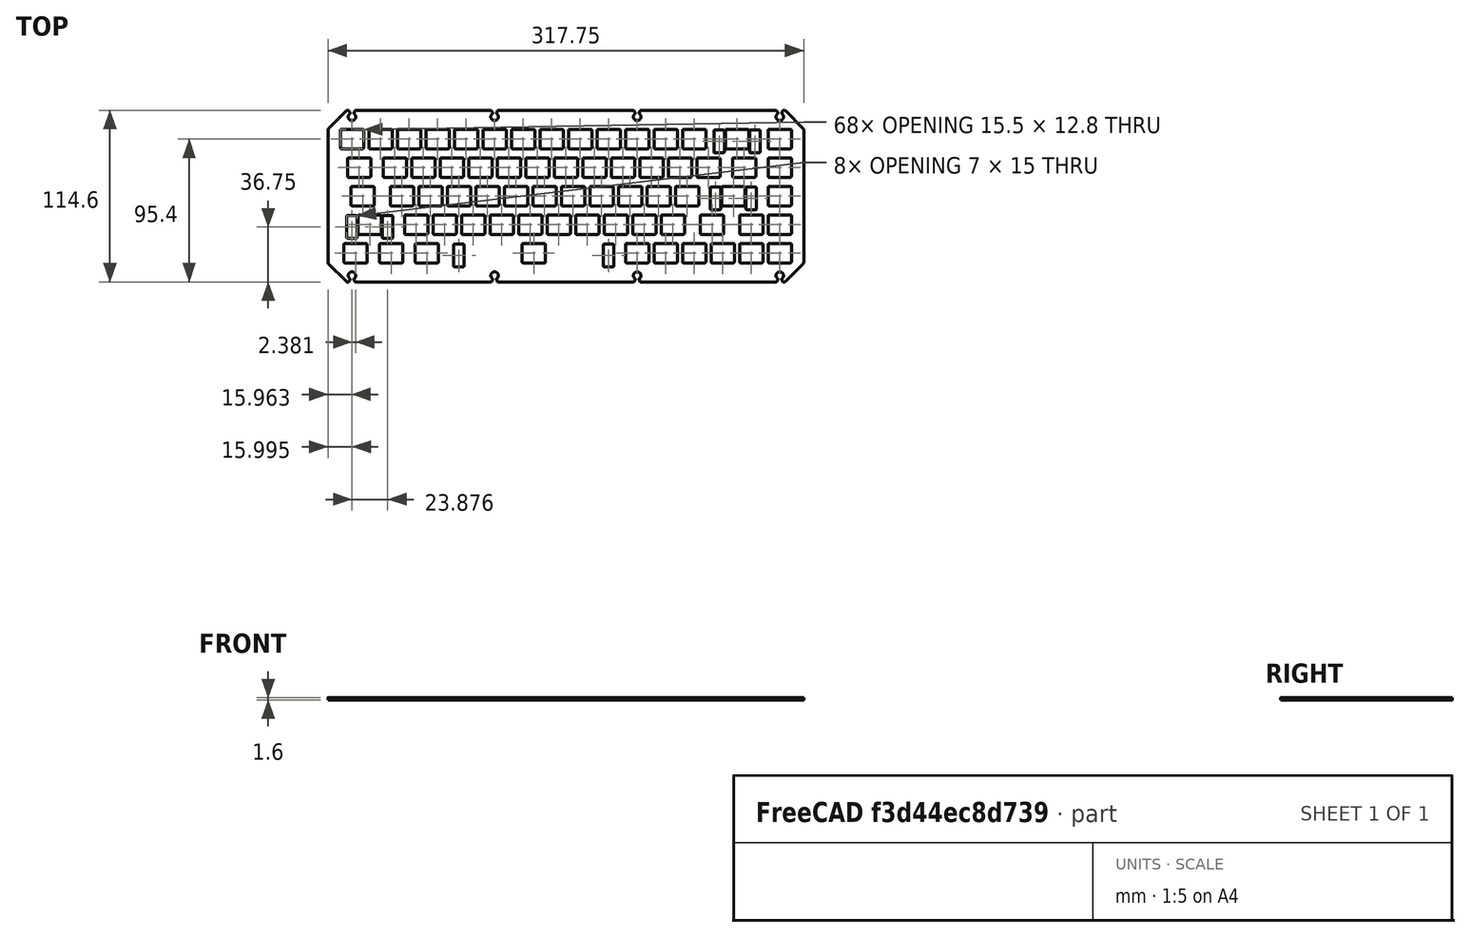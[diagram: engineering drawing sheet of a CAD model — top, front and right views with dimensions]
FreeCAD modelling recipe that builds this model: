
FCSTD DOCUMENT  (FreeCAD 0.21R33771 (Git))
Label: plate_merged
License: All rights reserved
LicenseURL: https://en.wikipedia.org/wiki/All_rights_reserved
objects: Sketcher::SketchObject×1, PartDesign::Pad×1, PartDesign::Body×1
note: 4 computed .brp shape members not serialized (recipe doc carries the construction recipe); baked Part::Feature solids carry a one-line shape summary decoded from their .brp

FEATURE [Sketcher::SketchObject] Sketch
  FullyConstrained = false
  MapMode = 5
  Support = -> [XY_Plane]
  sketch-geometry (688):
    g0: ArcOfCircle CenterX=-150.125 CenterY=44 CenterZ=0 NormalX=0 NormalY=0 NormalZ=1 AngleXU=0 Radius=0.5 StartAngle=1.5708 EndAngle=3.14159
    g1: LineSegment StartX=-150.125 StartY=44.5 StartZ=0 EndX=-135.625 EndY=44.5 EndZ=0
    g2: ArcOfCircle CenterX=-135.625 CenterY=44 CenterZ=0 NormalX=0 NormalY=0 NormalZ=1 AngleXU=0 Radius=0.5 StartAngle=0 EndAngle=1.5708
    g3: LineSegment StartX=-135.125 StartY=44 StartZ=0 EndX=-135.125 EndY=32.2 EndZ=0
    g4: ArcOfCircle CenterX=-135.625 CenterY=32.2 CenterZ=0 NormalX=0 NormalY=0 NormalZ=1 AngleXU=0 Radius=0.5 StartAngle=4.71239 EndAngle=6.28319
    g5: LineSegment StartX=-150.125 StartY=31.7 StartZ=0 EndX=-135.625 EndY=31.7 EndZ=0
    g6: ArcOfCircle CenterX=-150.125 CenterY=32.2 CenterZ=0 NormalX=0 NormalY=0 NormalZ=1 AngleXU=0 Radius=0.5 StartAngle=3.14159 EndAngle=4.71239
    g7: LineSegment StartX=-150.625 StartY=44 StartZ=0 EndX=-150.625 EndY=32.2 EndZ=0
    g8: ArcOfCircle CenterX=-131.075 CenterY=44 CenterZ=0 NormalX=0 NormalY=0 NormalZ=1 AngleXU=0 Radius=0.5 StartAngle=1.5708 EndAngle=3.14159
    g9: LineSegment StartX=-131.075 StartY=44.5 StartZ=0 EndX=-116.575 EndY=44.5 EndZ=0
    g10: ArcOfCircle CenterX=-116.575 CenterY=44 CenterZ=0 NormalX=0 NormalY=0 NormalZ=1 AngleXU=0 Radius=0.5 StartAngle=0 EndAngle=1.5708
    g11: LineSegment StartX=-116.075 StartY=44 StartZ=0 EndX=-116.075 EndY=32.2 EndZ=0
    g12: ArcOfCircle CenterX=-116.575 CenterY=32.2 CenterZ=0 NormalX=0 NormalY=0 NormalZ=1 AngleXU=0 Radius=0.5 StartAngle=4.71239 EndAngle=6.28319
    g13: LineSegment StartX=-131.075 StartY=31.7 StartZ=0 EndX=-116.575 EndY=31.7 EndZ=0
    g14: ArcOfCircle CenterX=-131.075 CenterY=32.2 CenterZ=0 NormalX=0 NormalY=0 NormalZ=1 AngleXU=0 Radius=0.5 StartAngle=3.14159 EndAngle=4.71239
    g15: LineSegment StartX=-131.575 StartY=44 StartZ=0 EndX=-131.575 EndY=32.2 EndZ=0
    g16: ArcOfCircle CenterX=-112.025 CenterY=44 CenterZ=0 NormalX=0 NormalY=0 NormalZ=1 AngleXU=0 Radius=0.5 StartAngle=1.5708 EndAngle=3.14159
    g17: LineSegment StartX=-112.025 StartY=44.5 StartZ=0 EndX=-97.525 EndY=44.5 EndZ=0
    g18: ArcOfCircle CenterX=-97.525 CenterY=44 CenterZ=0 NormalX=0 NormalY=0 NormalZ=1 AngleXU=0 Radius=0.5 StartAngle=0 EndAngle=1.5708
    g19: LineSegment StartX=-97.025 StartY=44 StartZ=0 EndX=-97.025 EndY=32.2 EndZ=0
    g20: ArcOfCircle CenterX=-97.525 CenterY=32.2 CenterZ=0 NormalX=0 NormalY=0 NormalZ=1 AngleXU=0 Radius=0.5 StartAngle=4.71239 EndAngle=6.28319
    g21: LineSegment StartX=-112.025 StartY=31.7 StartZ=0 EndX=-97.525 EndY=31.7 EndZ=0
    g22: ArcOfCircle CenterX=-112.025 CenterY=32.2 CenterZ=0 NormalX=0 NormalY=0 NormalZ=1 AngleXU=0 Radius=0.5 StartAngle=3.14159 EndAngle=4.71239
    g23: LineSegment StartX=-112.525 StartY=44 StartZ=0 EndX=-112.525 EndY=32.2 EndZ=0
    g24: ArcOfCircle CenterX=-92.975 CenterY=44 CenterZ=0 NormalX=0 NormalY=0 NormalZ=1 AngleXU=0 Radius=0.5 StartAngle=1.5708 EndAngle=3.14159
    g25: LineSegment StartX=-92.975 StartY=44.5 StartZ=0 EndX=-78.475 EndY=44.5 EndZ=0
    g26: ArcOfCircle CenterX=-78.475 CenterY=44 CenterZ=0 NormalX=0 NormalY=0 NormalZ=1 AngleXU=0 Radius=0.5 StartAngle=0 EndAngle=1.5708
    g27: LineSegment StartX=-77.975 StartY=44 StartZ=0 EndX=-77.975 EndY=32.2 EndZ=0
    g28: ArcOfCircle CenterX=-78.475 CenterY=32.2 CenterZ=0 NormalX=0 NormalY=0 NormalZ=1 AngleXU=0 Radius=0.5 StartAngle=4.71239 EndAngle=6.28319
    g29: LineSegment StartX=-92.975 StartY=31.7 StartZ=0 EndX=-78.475 EndY=31.7 EndZ=0
    g30: ArcOfCircle CenterX=-92.975 CenterY=32.2 CenterZ=0 NormalX=0 NormalY=0 NormalZ=1 AngleXU=0 Radius=0.5 StartAngle=3.14159 EndAngle=4.71239
    g31: LineSegment StartX=-93.475 StartY=44 StartZ=0 EndX=-93.475 EndY=32.2 EndZ=0
    g32: ArcOfCircle CenterX=-73.925 CenterY=44 CenterZ=0 NormalX=0 NormalY=0 NormalZ=1 AngleXU=0 Radius=0.5 StartAngle=1.5708 EndAngle=3.14159
    g33: LineSegment StartX=-73.925 StartY=44.5 StartZ=0 EndX=-59.425 EndY=44.5 EndZ=0
    g34: ArcOfCircle CenterX=-59.425 CenterY=44 CenterZ=0 NormalX=0 NormalY=0 NormalZ=1 AngleXU=0 Radius=0.5 StartAngle=0 EndAngle=1.5708
    g35: LineSegment StartX=-58.925 StartY=44 StartZ=0 EndX=-58.925 EndY=32.2 EndZ=0
    g36: ArcOfCircle CenterX=-59.425 CenterY=32.2 CenterZ=0 NormalX=0 NormalY=0 NormalZ=1 AngleXU=0 Radius=0.5 StartAngle=4.71239 EndAngle=6.28319
    g37: LineSegment StartX=-73.925 StartY=31.7 StartZ=0 EndX=-59.425 EndY=31.7 EndZ=0
    g38: ArcOfCircle CenterX=-73.925 CenterY=32.2 CenterZ=0 NormalX=0 NormalY=0 NormalZ=1 AngleXU=0 Radius=0.5 StartAngle=3.14159 EndAngle=4.71239
    g39: LineSegment StartX=-74.425 StartY=44 StartZ=0 EndX=-74.425 EndY=32.2 EndZ=0
    g40: ArcOfCircle CenterX=-54.875 CenterY=44 CenterZ=0 NormalX=0 NormalY=0 NormalZ=1 AngleXU=0 Radius=0.5 StartAngle=1.5708 EndAngle=3.14159
    g41: LineSegment StartX=-54.875 StartY=44.5 StartZ=0 EndX=-40.375 EndY=44.5 EndZ=0
    g42: ArcOfCircle CenterX=-40.375 CenterY=44 CenterZ=0 NormalX=0 NormalY=0 NormalZ=1 AngleXU=0 Radius=0.5 StartAngle=0 EndAngle=1.5708
    g43: LineSegment StartX=-39.875 StartY=44 StartZ=0 EndX=-39.875 EndY=32.2 EndZ=0
    g44: ArcOfCircle CenterX=-40.375 CenterY=32.2 CenterZ=0 NormalX=0 NormalY=0 NormalZ=1 AngleXU=0 Radius=0.5 StartAngle=4.71239 EndAngle=6.28319
    g45: LineSegment StartX=-54.875 StartY=31.7 StartZ=0 EndX=-40.375 EndY=31.7 EndZ=0
    g46: ArcOfCircle CenterX=-54.875 CenterY=32.2 CenterZ=0 NormalX=0 NormalY=0 NormalZ=1 AngleXU=0 Radius=0.5 StartAngle=3.14159 EndAngle=4.71239
    g47: LineSegment StartX=-55.375 StartY=44 StartZ=0 EndX=-55.375 EndY=32.2 EndZ=0
    g48: ArcOfCircle CenterX=-35.825 CenterY=44 CenterZ=0 NormalX=0 NormalY=0 NormalZ=1 AngleXU=0 Radius=0.5 StartAngle=1.5708 EndAngle=3.14159
    g49: LineSegment StartX=-35.825 StartY=44.5 StartZ=0 EndX=-21.325 EndY=44.5 EndZ=0
    g50: ArcOfCircle CenterX=-21.325 CenterY=44 CenterZ=0 NormalX=0 NormalY=0 NormalZ=1 AngleXU=0 Radius=0.5 StartAngle=0 EndAngle=1.5708
    g51: LineSegment StartX=-20.825 StartY=44 StartZ=0 EndX=-20.825 EndY=32.2 EndZ=0
    g52: ArcOfCircle CenterX=-21.325 CenterY=32.2 CenterZ=0 NormalX=0 NormalY=0 NormalZ=1 AngleXU=0 Radius=0.5 StartAngle=4.71239 EndAngle=6.28319
    g53: LineSegment StartX=-35.825 StartY=31.7 StartZ=0 EndX=-21.325 EndY=31.7 EndZ=0
    g54: ArcOfCircle CenterX=-35.825 CenterY=32.2 CenterZ=0 NormalX=0 NormalY=0 NormalZ=1 AngleXU=0 Radius=0.5 StartAngle=3.14159 EndAngle=4.71239
    g55: LineSegment StartX=-36.325 StartY=44 StartZ=0 EndX=-36.325 EndY=32.2 EndZ=0
    g56: ArcOfCircle CenterX=-16.775 CenterY=44 CenterZ=0 NormalX=0 NormalY=0 NormalZ=1 AngleXU=0 Radius=0.5 StartAngle=1.5708 EndAngle=3.14159
    g57: LineSegment StartX=-16.775 StartY=44.5 StartZ=0 EndX=-2.275 EndY=44.5 EndZ=0
    g58: ArcOfCircle CenterX=-2.275 CenterY=44 CenterZ=0 NormalX=0 NormalY=0 NormalZ=1 AngleXU=0 Radius=0.5 StartAngle=0 EndAngle=1.5708
    g59: LineSegment StartX=-1.775 StartY=44 StartZ=0 EndX=-1.775 EndY=32.2 EndZ=0
    g60: ArcOfCircle CenterX=-2.275 CenterY=32.2 CenterZ=0 NormalX=0 NormalY=0 NormalZ=1 AngleXU=0 Radius=0.5 StartAngle=4.71239 EndAngle=6.28319
    g61: LineSegment StartX=-16.775 StartY=31.7 StartZ=0 EndX=-2.275 EndY=31.7 EndZ=0
    g62: ArcOfCircle CenterX=-16.775 CenterY=32.2 CenterZ=0 NormalX=0 NormalY=0 NormalZ=1 AngleXU=0 Radius=0.5 StartAngle=3.14159 EndAngle=4.71239
    g63: LineSegment StartX=-17.275 StartY=44 StartZ=0 EndX=-17.275 EndY=32.2 EndZ=0
    g64: ArcOfCircle CenterX=2.275 CenterY=44 CenterZ=0 NormalX=0 NormalY=0 NormalZ=1 AngleXU=0 Radius=0.5 StartAngle=1.5708 EndAngle=3.14159
    g65: LineSegment StartX=2.275 StartY=44.5 StartZ=0 EndX=16.775 EndY=44.5 EndZ=0
    g66: ArcOfCircle CenterX=16.775 CenterY=44 CenterZ=0 NormalX=0 NormalY=0 NormalZ=1 AngleXU=0 Radius=0.5 StartAngle=0 EndAngle=1.5708
    g67: LineSegment StartX=17.275 StartY=44 StartZ=0 EndX=17.275 EndY=32.2 EndZ=0
    g68: ArcOfCircle CenterX=16.775 CenterY=32.2 CenterZ=0 NormalX=0 NormalY=0 NormalZ=1 AngleXU=0 Radius=0.5 StartAngle=4.71239 EndAngle=6.28319
    g69: LineSegment StartX=2.275 StartY=31.7 StartZ=0 EndX=16.775 EndY=31.7 EndZ=0
    g70: ArcOfCircle CenterX=2.275 CenterY=32.2 CenterZ=0 NormalX=0 NormalY=0 NormalZ=1 AngleXU=0 Radius=0.5 StartAngle=3.14159 EndAngle=4.71239
    g71: LineSegment StartX=1.775 StartY=44 StartZ=0 EndX=1.775 EndY=32.2 EndZ=0
    g72: ArcOfCircle CenterX=21.325 CenterY=44 CenterZ=0 NormalX=0 NormalY=0 NormalZ=1 AngleXU=0 Radius=0.5 StartAngle=1.5708 EndAngle=3.14159
    g73: LineSegment StartX=21.325 StartY=44.5 StartZ=0 EndX=35.825 EndY=44.5 EndZ=0
    g74: ArcOfCircle CenterX=35.825 CenterY=44 CenterZ=0 NormalX=0 NormalY=0 NormalZ=1 AngleXU=0 Radius=0.5 StartAngle=0 EndAngle=1.5708
    g75: LineSegment StartX=36.325 StartY=44 StartZ=0 EndX=36.325 EndY=32.2 EndZ=0
    g76: ArcOfCircle CenterX=35.825 CenterY=32.2 CenterZ=0 NormalX=0 NormalY=0 NormalZ=1 AngleXU=0 Radius=0.5 StartAngle=4.71239 EndAngle=6.28319
    g77: LineSegment StartX=21.325 StartY=31.7 StartZ=0 EndX=35.825 EndY=31.7 EndZ=0
    g78: ArcOfCircle CenterX=21.325 CenterY=32.2 CenterZ=0 NormalX=0 NormalY=0 NormalZ=1 AngleXU=0 Radius=0.5 StartAngle=3.14159 EndAngle=4.71239
    g79: LineSegment StartX=20.825 StartY=44 StartZ=0 EndX=20.825 EndY=32.2 EndZ=0
    g80: ArcOfCircle CenterX=40.375 CenterY=44 CenterZ=0 NormalX=0 NormalY=0 NormalZ=1 AngleXU=0 Radius=0.5 StartAngle=1.5708 EndAngle=3.14159
    g81: LineSegment StartX=40.375 StartY=44.5 StartZ=0 EndX=54.875 EndY=44.5 EndZ=0
    g82: ArcOfCircle CenterX=54.875 CenterY=44 CenterZ=0 NormalX=0 NormalY=0 NormalZ=1 AngleXU=0 Radius=0.5 StartAngle=0 EndAngle=1.5708
    g83: LineSegment StartX=55.375 StartY=44 StartZ=0 EndX=55.375 EndY=32.2 EndZ=0
    g84: ArcOfCircle CenterX=54.875 CenterY=32.2 CenterZ=0 NormalX=0 NormalY=0 NormalZ=1 AngleXU=0 Radius=0.5 StartAngle=4.71239 EndAngle=6.28319
    g85: LineSegment StartX=40.375 StartY=31.7 StartZ=0 EndX=54.875 EndY=31.7 EndZ=0
    g86: ArcOfCircle CenterX=40.375 CenterY=32.2 CenterZ=0 NormalX=0 NormalY=0 NormalZ=1 AngleXU=0 Radius=0.5 StartAngle=3.14159 EndAngle=4.71239
    g87: LineSegment StartX=39.875 StartY=44 StartZ=0 EndX=39.875 EndY=32.2 EndZ=0
    g88: ArcOfCircle CenterX=59.425 CenterY=44 CenterZ=0 NormalX=0 NormalY=0 NormalZ=1 AngleXU=0 Radius=0.5 StartAngle=1.5708 EndAngle=3.14159
    g89: LineSegment StartX=59.425 StartY=44.5 StartZ=0 EndX=73.925 EndY=44.5 EndZ=0
    g90: ArcOfCircle CenterX=73.925 CenterY=44 CenterZ=0 NormalX=0 NormalY=0 NormalZ=1 AngleXU=0 Radius=0.5 StartAngle=0 EndAngle=1.5708
    g91: LineSegment StartX=74.425 StartY=44 StartZ=0 EndX=74.425 EndY=32.2 EndZ=0
    g92: ArcOfCircle CenterX=73.925 CenterY=32.2 CenterZ=0 NormalX=0 NormalY=0 NormalZ=1 AngleXU=0 Radius=0.5 StartAngle=4.71239 EndAngle=6.28319
    g93: LineSegment StartX=59.425 StartY=31.7 StartZ=0 EndX=73.925 EndY=31.7 EndZ=0
    g94: ArcOfCircle CenterX=59.425 CenterY=32.2 CenterZ=0 NormalX=0 NormalY=0 NormalZ=1 AngleXU=0 Radius=0.5 StartAngle=3.14159 EndAngle=4.71239
    g95: LineSegment StartX=58.925 StartY=44 StartZ=0 EndX=58.925 EndY=32.2 EndZ=0
    g96: ArcOfCircle CenterX=78.475 CenterY=44 CenterZ=0 NormalX=0 NormalY=0 NormalZ=1 AngleXU=0 Radius=0.5 StartAngle=1.5708 EndAngle=3.14159
    g97: LineSegment StartX=78.475 StartY=44.5 StartZ=0 EndX=92.975 EndY=44.5 EndZ=0
    g98: ArcOfCircle CenterX=92.975 CenterY=44 CenterZ=0 NormalX=0 NormalY=0 NormalZ=1 AngleXU=0 Radius=0.5 StartAngle=0 EndAngle=1.5708
    g99: LineSegment StartX=93.475 StartY=44 StartZ=0 EndX=93.475 EndY=32.2 EndZ=0
    g100: ArcOfCircle CenterX=92.975 CenterY=32.2 CenterZ=0 NormalX=0 NormalY=0 NormalZ=1 AngleXU=0 Radius=0.5 StartAngle=4.71239 EndAngle=6.28319
    g101: LineSegment StartX=78.475 StartY=31.7 StartZ=0 EndX=92.975 EndY=31.7 EndZ=0
    g102: ArcOfCircle CenterX=78.475 CenterY=32.2 CenterZ=0 NormalX=0 NormalY=0 NormalZ=1 AngleXU=0 Radius=0.5 StartAngle=3.14159 EndAngle=4.71239
    g103: LineSegment StartX=77.975 StartY=44 StartZ=0 EndX=77.975 EndY=32.2 EndZ=0
    g104: ArcOfCircle CenterX=107.05 CenterY=44 CenterZ=0 NormalX=0 NormalY=0 NormalZ=1 AngleXU=0 Radius=0.5 StartAngle=1.5708 EndAngle=3.14159
    g105: LineSegment StartX=107.05 StartY=44.5 StartZ=0 EndX=121.55 EndY=44.5 EndZ=0
    g106: ArcOfCircle CenterX=121.55 CenterY=44 CenterZ=0 NormalX=0 NormalY=0 NormalZ=1 AngleXU=0 Radius=0.5 StartAngle=0 EndAngle=1.5708
    g107: LineSegment StartX=122.05 StartY=44 StartZ=0 EndX=122.05 EndY=32.2 EndZ=0
    g108: ArcOfCircle CenterX=121.55 CenterY=32.2 CenterZ=0 NormalX=0 NormalY=0 NormalZ=1 AngleXU=0 Radius=0.5 StartAngle=4.71239 EndAngle=6.28319
    g109: LineSegment StartX=107.05 StartY=31.7 StartZ=0 EndX=121.55 EndY=31.7 EndZ=0
    g110: ArcOfCircle CenterX=107.05 CenterY=32.2 CenterZ=0 NormalX=0 NormalY=0 NormalZ=1 AngleXU=0 Radius=0.5 StartAngle=3.14159 EndAngle=4.71239
    g111: LineSegment StartX=106.55 StartY=44 StartZ=0 EndX=106.55 EndY=32.2 EndZ=0
    g112: ArcOfCircle CenterX=99.362 CenterY=43.6 CenterZ=0 NormalX=0 NormalY=0 NormalZ=1 AngleXU=0 Radius=0.5 StartAngle=1.5708 EndAngle=3.14159
    g113: LineSegment StartX=99.362 StartY=44.1 StartZ=0 EndX=105.362 EndY=44.1 EndZ=0
    g114: ArcOfCircle CenterX=105.362 CenterY=43.6 CenterZ=0 NormalX=0 NormalY=0 NormalZ=1 AngleXU=0 Radius=0.5 StartAngle=0 EndAngle=1.5708
    g115: LineSegment StartX=105.862 StartY=43.6 StartZ=0 EndX=105.862 EndY=29.6 EndZ=0
    g116: ArcOfCircle CenterX=105.362 CenterY=29.6 CenterZ=0 NormalX=0 NormalY=0 NormalZ=1 AngleXU=0 Radius=0.5 StartAngle=4.71239 EndAngle=6.28319
    g117: LineSegment StartX=99.362 StartY=29.1 StartZ=0 EndX=105.362 EndY=29.1 EndZ=0
    g118: ArcOfCircle CenterX=99.362 CenterY=29.6 CenterZ=0 NormalX=0 NormalY=0 NormalZ=1 AngleXU=0 Radius=0.5 StartAngle=3.14159 EndAngle=4.71239
    g119: LineSegment StartX=98.862 StartY=43.6 StartZ=0 EndX=98.862 EndY=29.6 EndZ=0
    g120: ArcOfCircle CenterX=123.238 CenterY=43.6 CenterZ=0 NormalX=0 NormalY=0 NormalZ=1 AngleXU=0 Radius=0.5 StartAngle=1.5708 EndAngle=3.14159
    g121: LineSegment StartX=123.238 StartY=44.1 StartZ=0 EndX=129.238 EndY=44.1 EndZ=0
    g122: ArcOfCircle CenterX=129.238 CenterY=43.6 CenterZ=0 NormalX=0 NormalY=0 NormalZ=1 AngleXU=0 Radius=0.5 StartAngle=0 EndAngle=1.5708
    g123: LineSegment StartX=129.738 StartY=43.6 StartZ=0 EndX=129.738 EndY=29.6 EndZ=0
    g124: ArcOfCircle CenterX=129.238 CenterY=29.6 CenterZ=0 NormalX=0 NormalY=0 NormalZ=1 AngleXU=0 Radius=0.5 StartAngle=4.71239 EndAngle=6.28319
    g125: LineSegment StartX=123.238 StartY=29.1 StartZ=0 EndX=129.238 EndY=29.1 EndZ=0
    g126: ArcOfCircle CenterX=123.238 CenterY=29.6 CenterZ=0 NormalX=0 NormalY=0 NormalZ=1 AngleXU=0 Radius=0.5 StartAngle=3.14159 EndAngle=4.71239
    g127: LineSegment StartX=122.738 StartY=43.6 StartZ=0 EndX=122.738 EndY=29.6 EndZ=0
    g128: ArcOfCircle CenterX=135.625 CenterY=44 CenterZ=0 NormalX=0 NormalY=0 NormalZ=1 AngleXU=0 Radius=0.5 StartAngle=1.5708 EndAngle=3.14159
    g129: LineSegment StartX=135.625 StartY=44.5 StartZ=0 EndX=150.125 EndY=44.5 EndZ=0
    g130: ArcOfCircle CenterX=150.125 CenterY=44 CenterZ=0 NormalX=0 NormalY=0 NormalZ=1 AngleXU=0 Radius=0.5 StartAngle=0 EndAngle=1.5708
    g131: LineSegment StartX=150.625 StartY=44 StartZ=0 EndX=150.625 EndY=32.2 EndZ=0
    g132: ArcOfCircle CenterX=150.125 CenterY=32.2 CenterZ=0 NormalX=0 NormalY=0 NormalZ=1 AngleXU=0 Radius=0.5 StartAngle=4.71239 EndAngle=6.28319
    g133: LineSegment StartX=135.625 StartY=31.7 StartZ=0 EndX=150.125 EndY=31.7 EndZ=0
    g134: ArcOfCircle CenterX=135.625 CenterY=32.2 CenterZ=0 NormalX=0 NormalY=0 NormalZ=1 AngleXU=0 Radius=0.5 StartAngle=3.14159 EndAngle=4.71239
    g135: LineSegment StartX=135.125 StartY=44 StartZ=0 EndX=135.125 EndY=32.2 EndZ=0
    g136: ArcOfCircle CenterX=-145.363 CenterY=24.95 CenterZ=0 NormalX=0 NormalY=0 NormalZ=1 AngleXU=0 Radius=0.5 StartAngle=1.5708 EndAngle=3.14159
    g137: LineSegment StartX=-145.363 StartY=25.45 StartZ=0 EndX=-130.863 EndY=25.45 EndZ=0
    g138: ArcOfCircle CenterX=-130.863 CenterY=24.95 CenterZ=0 NormalX=0 NormalY=0 NormalZ=1 AngleXU=0 Radius=0.5 StartAngle=0 EndAngle=1.5708
    g139: LineSegment StartX=-130.363 StartY=24.95 StartZ=0 EndX=-130.363 EndY=13.15 EndZ=0
    g140: ArcOfCircle CenterX=-130.863 CenterY=13.15 CenterZ=0 NormalX=0 NormalY=0 NormalZ=1 AngleXU=0 Radius=0.5 StartAngle=4.71239 EndAngle=6.28319
    g141: LineSegment StartX=-145.363 StartY=12.65 StartZ=0 EndX=-130.863 EndY=12.65 EndZ=0
    g142: ArcOfCircle CenterX=-145.363 CenterY=13.15 CenterZ=0 NormalX=0 NormalY=0 NormalZ=1 AngleXU=0 Radius=0.5 StartAngle=3.14159 EndAngle=4.71239
    g143: LineSegment StartX=-145.863 StartY=24.95 StartZ=0 EndX=-145.863 EndY=13.15 EndZ=0
    g144: ArcOfCircle CenterX=-121.55 CenterY=24.95 CenterZ=0 NormalX=0 NormalY=0 NormalZ=1 AngleXU=0 Radius=0.5 StartAngle=1.5708 EndAngle=3.14159
    g145: LineSegment StartX=-121.55 StartY=25.45 StartZ=0 EndX=-107.05 EndY=25.45 EndZ=0
    g146: ArcOfCircle CenterX=-107.05 CenterY=24.95 CenterZ=0 NormalX=0 NormalY=0 NormalZ=1 AngleXU=0 Radius=0.5 StartAngle=0 EndAngle=1.5708
    g147: LineSegment StartX=-106.55 StartY=24.95 StartZ=0 EndX=-106.55 EndY=13.15 EndZ=0
    g148: ArcOfCircle CenterX=-107.05 CenterY=13.15 CenterZ=0 NormalX=0 NormalY=0 NormalZ=1 AngleXU=0 Radius=0.5 StartAngle=4.71239 EndAngle=6.28319
    g149: LineSegment StartX=-121.55 StartY=12.65 StartZ=0 EndX=-107.05 EndY=12.65 EndZ=0
    g150: ArcOfCircle CenterX=-121.55 CenterY=13.15 CenterZ=0 NormalX=0 NormalY=0 NormalZ=1 AngleXU=0 Radius=0.5 StartAngle=3.14159 EndAngle=4.71239
    g151: LineSegment StartX=-122.05 StartY=24.95 StartZ=0 EndX=-122.05 EndY=13.15 EndZ=0
    g152: ArcOfCircle CenterX=-102.5 CenterY=24.95 CenterZ=0 NormalX=0 NormalY=0 NormalZ=1 AngleXU=0 Radius=0.5 StartAngle=1.5708 EndAngle=3.14159
    g153: LineSegment StartX=-102.5 StartY=25.45 StartZ=0 EndX=-88 EndY=25.45 EndZ=0
    g154: ArcOfCircle CenterX=-88 CenterY=24.95 CenterZ=0 NormalX=0 NormalY=0 NormalZ=1 AngleXU=0 Radius=0.5 StartAngle=0 EndAngle=1.5708
    g155: LineSegment StartX=-87.5 StartY=24.95 StartZ=0 EndX=-87.5 EndY=13.15 EndZ=0
    g156: ArcOfCircle CenterX=-88 CenterY=13.15 CenterZ=0 NormalX=0 NormalY=0 NormalZ=1 AngleXU=0 Radius=0.5 StartAngle=4.71239 EndAngle=6.28319
    g157: LineSegment StartX=-102.5 StartY=12.65 StartZ=0 EndX=-88 EndY=12.65 EndZ=0
    g158: ArcOfCircle CenterX=-102.5 CenterY=13.15 CenterZ=0 NormalX=0 NormalY=0 NormalZ=1 AngleXU=0 Radius=0.5 StartAngle=3.14159 EndAngle=4.71239
    g159: LineSegment StartX=-103 StartY=24.95 StartZ=0 EndX=-103 EndY=13.15 EndZ=0
    g160: ArcOfCircle CenterX=-83.45 CenterY=24.95 CenterZ=0 NormalX=0 NormalY=0 NormalZ=1 AngleXU=0 Radius=0.5 StartAngle=1.5708 EndAngle=3.14159
    g161: LineSegment StartX=-83.45 StartY=25.45 StartZ=0 EndX=-68.95 EndY=25.45 EndZ=0
    g162: ArcOfCircle CenterX=-68.95 CenterY=24.95 CenterZ=0 NormalX=0 NormalY=0 NormalZ=1 AngleXU=0 Radius=0.5 StartAngle=0 EndAngle=1.5708
    g163: LineSegment StartX=-68.45 StartY=24.95 StartZ=0 EndX=-68.45 EndY=13.15 EndZ=0
    g164: ArcOfCircle CenterX=-68.95 CenterY=13.15 CenterZ=0 NormalX=0 NormalY=0 NormalZ=1 AngleXU=0 Radius=0.5 StartAngle=4.71239 EndAngle=6.28319
    g165: LineSegment StartX=-83.45 StartY=12.65 StartZ=0 EndX=-68.95 EndY=12.65 EndZ=0
    g166: ArcOfCircle CenterX=-83.45 CenterY=13.15 CenterZ=0 NormalX=0 NormalY=0 NormalZ=1 AngleXU=0 Radius=0.5 StartAngle=3.14159 EndAngle=4.71239
    g167: LineSegment StartX=-83.95 StartY=24.95 StartZ=0 EndX=-83.95 EndY=13.15 EndZ=0
    g168: ArcOfCircle CenterX=-64.4 CenterY=24.95 CenterZ=0 NormalX=0 NormalY=0 NormalZ=1 AngleXU=0 Radius=0.5 StartAngle=1.5708 EndAngle=3.14159
    g169: LineSegment StartX=-64.4 StartY=25.45 StartZ=0 EndX=-49.9 EndY=25.45 EndZ=0
    g170: ArcOfCircle CenterX=-49.9 CenterY=24.95 CenterZ=0 NormalX=0 NormalY=0 NormalZ=1 AngleXU=0 Radius=0.5 StartAngle=0 EndAngle=1.5708
    g171: LineSegment StartX=-49.4 StartY=24.95 StartZ=0 EndX=-49.4 EndY=13.15 EndZ=0
    g172: ArcOfCircle CenterX=-49.9 CenterY=13.15 CenterZ=0 NormalX=0 NormalY=0 NormalZ=1 AngleXU=0 Radius=0.5 StartAngle=4.71239 EndAngle=6.28319
    g173: LineSegment StartX=-64.4 StartY=12.65 StartZ=0 EndX=-49.9 EndY=12.65 EndZ=0
    g174: ArcOfCircle CenterX=-64.4 CenterY=13.15 CenterZ=0 NormalX=0 NormalY=0 NormalZ=1 AngleXU=0 Radius=0.5 StartAngle=3.14159 EndAngle=4.71239
    g175: LineSegment StartX=-64.9 StartY=24.95 StartZ=0 EndX=-64.9 EndY=13.15 EndZ=0
    g176: ArcOfCircle CenterX=-45.35 CenterY=24.95 CenterZ=0 NormalX=0 NormalY=0 NormalZ=1 AngleXU=0 Radius=0.5 StartAngle=1.5708 EndAngle=3.14159
    g177: LineSegment StartX=-45.35 StartY=25.45 StartZ=0 EndX=-30.85 EndY=25.45 EndZ=0
    g178: ArcOfCircle CenterX=-30.85 CenterY=24.95 CenterZ=0 NormalX=0 NormalY=0 NormalZ=1 AngleXU=0 Radius=0.5 StartAngle=0 EndAngle=1.5708
    g179: LineSegment StartX=-30.35 StartY=24.95 StartZ=0 EndX=-30.35 EndY=13.15 EndZ=0
    g180: ArcOfCircle CenterX=-30.85 CenterY=13.15 CenterZ=0 NormalX=0 NormalY=0 NormalZ=1 AngleXU=0 Radius=0.5 StartAngle=4.71239 EndAngle=6.28319
    g181: LineSegment StartX=-45.35 StartY=12.65 StartZ=0 EndX=-30.85 EndY=12.65 EndZ=0
    g182: ArcOfCircle CenterX=-45.35 CenterY=13.15 CenterZ=0 NormalX=0 NormalY=0 NormalZ=1 AngleXU=0 Radius=0.5 StartAngle=3.14159 EndAngle=4.71239
    g183: LineSegment StartX=-45.85 StartY=24.95 StartZ=0 EndX=-45.85 EndY=13.15 EndZ=0
    g184: ArcOfCircle CenterX=-26.3 CenterY=24.95 CenterZ=0 NormalX=0 NormalY=0 NormalZ=1 AngleXU=0 Radius=0.5 StartAngle=1.5708 EndAngle=3.14159
    g185: LineSegment StartX=-26.3 StartY=25.45 StartZ=0 EndX=-11.8 EndY=25.45 EndZ=0
    g186: ArcOfCircle CenterX=-11.8 CenterY=24.95 CenterZ=0 NormalX=0 NormalY=0 NormalZ=1 AngleXU=0 Radius=0.5 StartAngle=0 EndAngle=1.5708
    g187: LineSegment StartX=-11.3 StartY=24.95 StartZ=0 EndX=-11.3 EndY=13.15 EndZ=0
    g188: ArcOfCircle CenterX=-11.8 CenterY=13.15 CenterZ=0 NormalX=0 NormalY=0 NormalZ=1 AngleXU=0 Radius=0.5 StartAngle=4.71239 EndAngle=6.28319
    g189: LineSegment StartX=-26.3 StartY=12.65 StartZ=0 EndX=-11.8 EndY=12.65 EndZ=0
    g190: ArcOfCircle CenterX=-26.3 CenterY=13.15 CenterZ=0 NormalX=0 NormalY=0 NormalZ=1 AngleXU=0 Radius=0.5 StartAngle=3.14159 EndAngle=4.71239
    g191: LineSegment StartX=-26.8 StartY=24.95 StartZ=0 EndX=-26.8 EndY=13.15 EndZ=0
    g192: ArcOfCircle CenterX=-7.25 CenterY=24.95 CenterZ=0 NormalX=0 NormalY=0 NormalZ=1 AngleXU=0 Radius=0.5 StartAngle=1.5708 EndAngle=3.14159
    g193: LineSegment StartX=-7.25 StartY=25.45 StartZ=0 EndX=7.25 EndY=25.45 EndZ=0
    g194: ArcOfCircle CenterX=7.25 CenterY=24.95 CenterZ=0 NormalX=0 NormalY=0 NormalZ=1 AngleXU=0 Radius=0.5 StartAngle=0 EndAngle=1.5708
    g195: LineSegment StartX=7.75 StartY=24.95 StartZ=0 EndX=7.75 EndY=13.15 EndZ=0
    g196: ArcOfCircle CenterX=7.25 CenterY=13.15 CenterZ=0 NormalX=0 NormalY=0 NormalZ=1 AngleXU=0 Radius=0.5 StartAngle=4.71239 EndAngle=6.28319
    g197: LineSegment StartX=-7.25 StartY=12.65 StartZ=0 EndX=7.25 EndY=12.65 EndZ=0
    g198: ArcOfCircle CenterX=-7.25 CenterY=13.15 CenterZ=0 NormalX=0 NormalY=0 NormalZ=1 AngleXU=0 Radius=0.5 StartAngle=3.14159 EndAngle=4.71239
    g199: LineSegment StartX=-7.75 StartY=24.95 StartZ=0 EndX=-7.75 EndY=13.15 EndZ=0
    g200: ArcOfCircle CenterX=11.8 CenterY=24.95 CenterZ=0 NormalX=0 NormalY=0 NormalZ=1 AngleXU=0 Radius=0.5 StartAngle=1.5708 EndAngle=3.14159
    g201: LineSegment StartX=11.8 StartY=25.45 StartZ=0 EndX=26.3 EndY=25.45 EndZ=0
    g202: ArcOfCircle CenterX=26.3 CenterY=24.95 CenterZ=0 NormalX=0 NormalY=0 NormalZ=1 AngleXU=0 Radius=0.5 StartAngle=0 EndAngle=1.5708
    g203: LineSegment StartX=26.8 StartY=24.95 StartZ=0 EndX=26.8 EndY=13.15 EndZ=0
    g204: ArcOfCircle CenterX=26.3 CenterY=13.15 CenterZ=0 NormalX=0 NormalY=0 NormalZ=1 AngleXU=0 Radius=0.5 StartAngle=4.71239 EndAngle=6.28319
    g205: LineSegment StartX=11.8 StartY=12.65 StartZ=0 EndX=26.3 EndY=12.65 EndZ=0
    g206: ArcOfCircle CenterX=11.8 CenterY=13.15 CenterZ=0 NormalX=0 NormalY=0 NormalZ=1 AngleXU=0 Radius=0.5 StartAngle=3.14159 EndAngle=4.71239
    g207: LineSegment StartX=11.3 StartY=24.95 StartZ=0 EndX=11.3 EndY=13.15 EndZ=0
    g208: ArcOfCircle CenterX=30.85 CenterY=24.95 CenterZ=0 NormalX=0 NormalY=0 NormalZ=1 AngleXU=0 Radius=0.5 StartAngle=1.5708 EndAngle=3.14159
    g209: LineSegment StartX=30.85 StartY=25.45 StartZ=0 EndX=45.35 EndY=25.45 EndZ=0
    g210: ArcOfCircle CenterX=45.35 CenterY=24.95 CenterZ=0 NormalX=0 NormalY=0 NormalZ=1 AngleXU=0 Radius=0.5 StartAngle=0 EndAngle=1.5708
    g211: LineSegment StartX=45.85 StartY=24.95 StartZ=0 EndX=45.85 EndY=13.15 EndZ=0
    g212: ArcOfCircle CenterX=45.35 CenterY=13.15 CenterZ=0 NormalX=0 NormalY=0 NormalZ=1 AngleXU=0 Radius=0.5 StartAngle=4.71239 EndAngle=6.28319
    g213: LineSegment StartX=30.85 StartY=12.65 StartZ=0 EndX=45.35 EndY=12.65 EndZ=0
    g214: ArcOfCircle CenterX=30.85 CenterY=13.15 CenterZ=0 NormalX=0 NormalY=0 NormalZ=1 AngleXU=0 Radius=0.5 StartAngle=3.14159 EndAngle=4.71239
    g215: LineSegment StartX=30.35 StartY=24.95 StartZ=0 EndX=30.35 EndY=13.15 EndZ=0
    g216: ArcOfCircle CenterX=49.9 CenterY=24.95 CenterZ=0 NormalX=0 NormalY=0 NormalZ=1 AngleXU=0 Radius=0.5 StartAngle=1.5708 EndAngle=3.14159
    g217: LineSegment StartX=49.9 StartY=25.45 StartZ=0 EndX=64.4 EndY=25.45 EndZ=0
    g218: ArcOfCircle CenterX=64.4 CenterY=24.95 CenterZ=0 NormalX=0 NormalY=0 NormalZ=1 AngleXU=0 Radius=0.5 StartAngle=0 EndAngle=1.5708
    g219: LineSegment StartX=64.9 StartY=24.95 StartZ=0 EndX=64.9 EndY=13.15 EndZ=0
    g220: ArcOfCircle CenterX=64.4 CenterY=13.15 CenterZ=0 NormalX=0 NormalY=0 NormalZ=1 AngleXU=0 Radius=0.5 StartAngle=4.71239 EndAngle=6.28319
    g221: LineSegment StartX=49.9 StartY=12.65 StartZ=0 EndX=64.4 EndY=12.65 EndZ=0
    g222: ArcOfCircle CenterX=49.9 CenterY=13.15 CenterZ=0 NormalX=0 NormalY=0 NormalZ=1 AngleXU=0 Radius=0.5 StartAngle=3.14159 EndAngle=4.71239
    g223: LineSegment StartX=49.4 StartY=24.95 StartZ=0 EndX=49.4 EndY=13.15 EndZ=0
    g224: ArcOfCircle CenterX=68.95 CenterY=24.95 CenterZ=0 NormalX=0 NormalY=0 NormalZ=1 AngleXU=0 Radius=0.5 StartAngle=1.5708 EndAngle=3.14159
    g225: LineSegment StartX=68.95 StartY=25.45 StartZ=0 EndX=83.45 EndY=25.45 EndZ=0
    g226: ArcOfCircle CenterX=83.45 CenterY=24.95 CenterZ=0 NormalX=0 NormalY=0 NormalZ=1 AngleXU=0 Radius=0.5 StartAngle=0 EndAngle=1.5708
    g227: LineSegment StartX=83.95 StartY=24.95 StartZ=0 EndX=83.95 EndY=13.15 EndZ=0
    g228: ArcOfCircle CenterX=83.45 CenterY=13.15 CenterZ=0 NormalX=0 NormalY=0 NormalZ=1 AngleXU=0 Radius=0.5 StartAngle=4.71239 EndAngle=6.28319
    g229: LineSegment StartX=68.95 StartY=12.65 StartZ=0 EndX=83.45 EndY=12.65 EndZ=0
    g230: ArcOfCircle CenterX=68.95 CenterY=13.15 CenterZ=0 NormalX=0 NormalY=0 NormalZ=1 AngleXU=0 Radius=0.5 StartAngle=3.14159 EndAngle=4.71239
    g231: LineSegment StartX=68.45 StartY=24.95 StartZ=0 EndX=68.45 EndY=13.15 EndZ=0
    g232: ArcOfCircle CenterX=88 CenterY=24.95 CenterZ=0 NormalX=0 NormalY=0 NormalZ=1 AngleXU=0 Radius=0.5 StartAngle=1.5708 EndAngle=3.14159
    g233: LineSegment StartX=88 StartY=25.45 StartZ=0 EndX=102.5 EndY=25.45 EndZ=0
    g234: ArcOfCircle CenterX=102.5 CenterY=24.95 CenterZ=0 NormalX=0 NormalY=0 NormalZ=1 AngleXU=0 Radius=0.5 StartAngle=0 EndAngle=1.5708
    g235: LineSegment StartX=103 StartY=24.95 StartZ=0 EndX=103 EndY=13.15 EndZ=0
    g236: ArcOfCircle CenterX=102.5 CenterY=13.15 CenterZ=0 NormalX=0 NormalY=0 NormalZ=1 AngleXU=0 Radius=0.5 StartAngle=4.71239 EndAngle=6.28319
    g237: LineSegment StartX=88 StartY=12.65 StartZ=0 EndX=102.5 EndY=12.65 EndZ=0
    g238: ArcOfCircle CenterX=88 CenterY=13.15 CenterZ=0 NormalX=0 NormalY=0 NormalZ=1 AngleXU=0 Radius=0.5 StartAngle=3.14159 EndAngle=4.71239
    g239: LineSegment StartX=87.5 StartY=24.95 StartZ=0 EndX=87.5 EndY=13.15 EndZ=0
    g240: ArcOfCircle CenterX=111.812 CenterY=24.95 CenterZ=0 NormalX=0 NormalY=0 NormalZ=1 AngleXU=0 Radius=0.5 StartAngle=1.5708 EndAngle=3.14159
    g241: LineSegment StartX=111.812 StartY=25.45 StartZ=0 EndX=126.312 EndY=25.45 EndZ=0
    g242: ArcOfCircle CenterX=126.312 CenterY=24.95 CenterZ=0 NormalX=0 NormalY=0 NormalZ=1 AngleXU=0 Radius=0.5 StartAngle=0 EndAngle=1.5708
    g243: LineSegment StartX=126.812 StartY=24.95 StartZ=0 EndX=126.812 EndY=13.15 EndZ=0
    g244: ArcOfCircle CenterX=126.312 CenterY=13.15 CenterZ=0 NormalX=0 NormalY=0 NormalZ=1 AngleXU=0 Radius=0.5 StartAngle=4.71239 EndAngle=6.28319
    g245: LineSegment StartX=111.812 StartY=12.65 StartZ=0 EndX=126.312 EndY=12.65 EndZ=0
    g246: ArcOfCircle CenterX=111.812 CenterY=13.15 CenterZ=0 NormalX=0 NormalY=0 NormalZ=1 AngleXU=0 Radius=0.5 StartAngle=3.14159 EndAngle=4.71239
    g247: LineSegment StartX=111.312 StartY=24.95 StartZ=0 EndX=111.312 EndY=13.15 EndZ=0
    g248: ArcOfCircle CenterX=135.625 CenterY=24.95 CenterZ=0 NormalX=0 NormalY=0 NormalZ=1 AngleXU=0 Radius=0.5 StartAngle=1.5708 EndAngle=3.14159
    g249: LineSegment StartX=135.625 StartY=25.45 StartZ=0 EndX=150.125 EndY=25.45 EndZ=0
    g250: ArcOfCircle CenterX=150.125 CenterY=24.95 CenterZ=0 NormalX=0 NormalY=0 NormalZ=1 AngleXU=0 Radius=0.5 StartAngle=0 EndAngle=1.5708
    g251: LineSegment StartX=150.625 StartY=24.95 StartZ=0 EndX=150.625 EndY=13.15 EndZ=0
    g252: ArcOfCircle CenterX=150.125 CenterY=13.15 CenterZ=0 NormalX=0 NormalY=0 NormalZ=1 AngleXU=0 Radius=0.5 StartAngle=4.71239 EndAngle=6.28319
    g253: LineSegment StartX=135.625 StartY=12.65 StartZ=0 EndX=150.125 EndY=12.65 EndZ=0
    g254: ArcOfCircle CenterX=135.625 CenterY=13.15 CenterZ=0 NormalX=0 NormalY=0 NormalZ=1 AngleXU=0 Radius=0.5 StartAngle=3.14159 EndAngle=4.71239
    g255: LineSegment StartX=135.125 StartY=24.95 StartZ=0 EndX=135.125 EndY=13.15 EndZ=0
    g256: ArcOfCircle CenterX=-142.981 CenterY=5.9 CenterZ=0 NormalX=0 NormalY=0 NormalZ=1 AngleXU=0 Radius=0.5 StartAngle=1.5708 EndAngle=3.14159
    g257: LineSegment StartX=-142.981 StartY=6.4 StartZ=0 EndX=-128.481 EndY=6.4 EndZ=0
    g258: ArcOfCircle CenterX=-128.481 CenterY=5.9 CenterZ=0 NormalX=0 NormalY=0 NormalZ=1 AngleXU=0 Radius=0.5 StartAngle=0 EndAngle=1.5708
    g259: LineSegment StartX=-127.981 StartY=5.9 StartZ=0 EndX=-127.981 EndY=-5.9 EndZ=0
    g260: ArcOfCircle CenterX=-128.481 CenterY=-5.9 CenterZ=0 NormalX=0 NormalY=0 NormalZ=1 AngleXU=0 Radius=0.5 StartAngle=4.71239 EndAngle=6.28319
    g261: LineSegment StartX=-142.981 StartY=-6.4 StartZ=0 EndX=-128.481 EndY=-6.4 EndZ=0
    g262: ArcOfCircle CenterX=-142.981 CenterY=-5.9 CenterZ=0 NormalX=0 NormalY=0 NormalZ=1 AngleXU=0 Radius=0.5 StartAngle=3.14159 EndAngle=4.71239
    g263: LineSegment StartX=-143.481 StartY=5.9 StartZ=0 EndX=-143.481 EndY=-5.9 EndZ=0
    g264: ArcOfCircle CenterX=-116.788 CenterY=5.9 CenterZ=0 NormalX=0 NormalY=0 NormalZ=1 AngleXU=0 Radius=0.5 StartAngle=1.5708 EndAngle=3.14159
    g265: LineSegment StartX=-116.788 StartY=6.4 StartZ=0 EndX=-102.288 EndY=6.4 EndZ=0
    g266: ArcOfCircle CenterX=-102.288 CenterY=5.9 CenterZ=0 NormalX=0 NormalY=0 NormalZ=1 AngleXU=0 Radius=0.5 StartAngle=0 EndAngle=1.5708
    g267: LineSegment StartX=-101.788 StartY=5.9 StartZ=0 EndX=-101.788 EndY=-5.9 EndZ=0
    g268: ArcOfCircle CenterX=-102.288 CenterY=-5.9 CenterZ=0 NormalX=0 NormalY=0 NormalZ=1 AngleXU=0 Radius=0.5 StartAngle=4.71239 EndAngle=6.28319
    g269: LineSegment StartX=-116.788 StartY=-6.4 StartZ=0 EndX=-102.288 EndY=-6.4 EndZ=0
    g270: ArcOfCircle CenterX=-116.788 CenterY=-5.9 CenterZ=0 NormalX=0 NormalY=0 NormalZ=1 AngleXU=0 Radius=0.5 StartAngle=3.14159 EndAngle=4.71239
    g271: LineSegment StartX=-117.288 StartY=5.9 StartZ=0 EndX=-117.288 EndY=-5.9 EndZ=0
    g272: ArcOfCircle CenterX=-97.7375 CenterY=5.9 CenterZ=0 NormalX=0 NormalY=0 NormalZ=1 AngleXU=0 Radius=0.5 StartAngle=1.5708 EndAngle=3.14159
    g273: LineSegment StartX=-97.7375 StartY=6.4 StartZ=0 EndX=-83.2375 EndY=6.4 EndZ=0
    g274: ArcOfCircle CenterX=-83.2375 CenterY=5.9 CenterZ=0 NormalX=0 NormalY=0 NormalZ=1 AngleXU=0 Radius=0.5 StartAngle=0 EndAngle=1.5708
    g275: LineSegment StartX=-82.7375 StartY=5.9 StartZ=0 EndX=-82.7375 EndY=-5.9 EndZ=0
    g276: ArcOfCircle CenterX=-83.2375 CenterY=-5.9 CenterZ=0 NormalX=0 NormalY=0 NormalZ=1 AngleXU=0 Radius=0.5 StartAngle=4.71239 EndAngle=6.28319
    g277: LineSegment StartX=-97.7375 StartY=-6.4 StartZ=0 EndX=-83.2375 EndY=-6.4 EndZ=0
    g278: ArcOfCircle CenterX=-97.7375 CenterY=-5.9 CenterZ=0 NormalX=0 NormalY=0 NormalZ=1 AngleXU=0 Radius=0.5 StartAngle=3.14159 EndAngle=4.71239
    g279: LineSegment StartX=-98.2375 StartY=5.9 StartZ=0 EndX=-98.2375 EndY=-5.9 EndZ=0
    g280: ArcOfCircle CenterX=-78.6875 CenterY=5.9 CenterZ=0 NormalX=0 NormalY=0 NormalZ=1 AngleXU=0 Radius=0.5 StartAngle=1.5708 EndAngle=3.14159
    g281: LineSegment StartX=-78.6875 StartY=6.4 StartZ=0 EndX=-64.1875 EndY=6.4 EndZ=0
    g282: ArcOfCircle CenterX=-64.1875 CenterY=5.9 CenterZ=0 NormalX=0 NormalY=0 NormalZ=1 AngleXU=0 Radius=0.5 StartAngle=0 EndAngle=1.5708
    g283: LineSegment StartX=-63.6875 StartY=5.9 StartZ=0 EndX=-63.6875 EndY=-5.9 EndZ=0
    g284: ArcOfCircle CenterX=-64.1875 CenterY=-5.9 CenterZ=0 NormalX=0 NormalY=0 NormalZ=1 AngleXU=0 Radius=0.5 StartAngle=4.71239 EndAngle=6.28319
    g285: LineSegment StartX=-78.6875 StartY=-6.4 StartZ=0 EndX=-64.1875 EndY=-6.4 EndZ=0
    g286: ArcOfCircle CenterX=-78.6875 CenterY=-5.9 CenterZ=0 NormalX=0 NormalY=0 NormalZ=1 AngleXU=0 Radius=0.5 StartAngle=3.14159 EndAngle=4.71239
    g287: LineSegment StartX=-79.1875 StartY=5.9 StartZ=0 EndX=-79.1875 EndY=-5.9 EndZ=0
    g288: ArcOfCircle CenterX=-59.6375 CenterY=5.9 CenterZ=0 NormalX=0 NormalY=0 NormalZ=1 AngleXU=0 Radius=0.5 StartAngle=1.5708 EndAngle=3.14159
    g289: LineSegment StartX=-59.6375 StartY=6.4 StartZ=0 EndX=-45.1375 EndY=6.4 EndZ=0
    g290: ArcOfCircle CenterX=-45.1375 CenterY=5.9 CenterZ=0 NormalX=0 NormalY=0 NormalZ=1 AngleXU=0 Radius=0.5 StartAngle=0 EndAngle=1.5708
    g291: LineSegment StartX=-44.6375 StartY=5.9 StartZ=0 EndX=-44.6375 EndY=-5.9 EndZ=0
    g292: ArcOfCircle CenterX=-45.1375 CenterY=-5.9 CenterZ=0 NormalX=0 NormalY=0 NormalZ=1 AngleXU=0 Radius=0.5 StartAngle=4.71239 EndAngle=6.28319
    g293: LineSegment StartX=-59.6375 StartY=-6.4 StartZ=0 EndX=-45.1375 EndY=-6.4 EndZ=0
    g294: ArcOfCircle CenterX=-59.6375 CenterY=-5.9 CenterZ=0 NormalX=0 NormalY=0 NormalZ=1 AngleXU=0 Radius=0.5 StartAngle=3.14159 EndAngle=4.71239
    g295: LineSegment StartX=-60.1375 StartY=5.9 StartZ=0 EndX=-60.1375 EndY=-5.9 EndZ=0
    g296: ArcOfCircle CenterX=-40.5875 CenterY=5.9 CenterZ=0 NormalX=0 NormalY=0 NormalZ=1 AngleXU=0 Radius=0.5 StartAngle=1.5708 EndAngle=3.14159
    g297: LineSegment StartX=-40.5875 StartY=6.4 StartZ=0 EndX=-26.0875 EndY=6.4 EndZ=0
    g298: ArcOfCircle CenterX=-26.0875 CenterY=5.9 CenterZ=0 NormalX=0 NormalY=0 NormalZ=1 AngleXU=0 Radius=0.5 StartAngle=0 EndAngle=1.5708
    g299: LineSegment StartX=-25.5875 StartY=5.9 StartZ=0 EndX=-25.5875 EndY=-5.9 EndZ=0
    g300: ArcOfCircle CenterX=-26.0875 CenterY=-5.9 CenterZ=0 NormalX=0 NormalY=0 NormalZ=1 AngleXU=0 Radius=0.5 StartAngle=4.71239 EndAngle=6.28319
    g301: LineSegment StartX=-40.5875 StartY=-6.4 StartZ=0 EndX=-26.0875 EndY=-6.4 EndZ=0
    g302: ArcOfCircle CenterX=-40.5875 CenterY=-5.9 CenterZ=0 NormalX=0 NormalY=0 NormalZ=1 AngleXU=0 Radius=0.5 StartAngle=3.14159 EndAngle=4.71239
    g303: LineSegment StartX=-41.0875 StartY=5.9 StartZ=0 EndX=-41.0875 EndY=-5.9 EndZ=0
    g304: ArcOfCircle CenterX=-21.5375 CenterY=5.9 CenterZ=0 NormalX=0 NormalY=0 NormalZ=1 AngleXU=0 Radius=0.5 StartAngle=1.5708 EndAngle=3.14159
    g305: LineSegment StartX=-21.5375 StartY=6.4 StartZ=0 EndX=-7.0375 EndY=6.4 EndZ=0
    g306: ArcOfCircle CenterX=-7.0375 CenterY=5.9 CenterZ=0 NormalX=0 NormalY=0 NormalZ=1 AngleXU=0 Radius=0.5 StartAngle=0 EndAngle=1.5708
    g307: LineSegment StartX=-6.5375 StartY=5.9 StartZ=0 EndX=-6.5375 EndY=-5.9 EndZ=0
    g308: ArcOfCircle CenterX=-7.0375 CenterY=-5.9 CenterZ=0 NormalX=0 NormalY=0 NormalZ=1 AngleXU=0 Radius=0.5 StartAngle=4.71239 EndAngle=6.28319
    g309: LineSegment StartX=-21.5375 StartY=-6.4 StartZ=0 EndX=-7.0375 EndY=-6.4 EndZ=0
    g310: ArcOfCircle CenterX=-21.5375 CenterY=-5.9 CenterZ=0 NormalX=0 NormalY=0 NormalZ=1 AngleXU=0 Radius=0.5 StartAngle=3.14159 EndAngle=4.71239
    g311: LineSegment StartX=-22.0375 StartY=5.9 StartZ=0 EndX=-22.0375 EndY=-5.9 EndZ=0
    g312: ArcOfCircle CenterX=-2.4875 CenterY=5.9 CenterZ=0 NormalX=0 NormalY=0 NormalZ=1 AngleXU=0 Radius=0.5 StartAngle=1.5708 EndAngle=3.14159
    g313: LineSegment StartX=-2.4875 StartY=6.4 StartZ=0 EndX=12.0125 EndY=6.4 EndZ=0
    g314: ArcOfCircle CenterX=12.0125 CenterY=5.9 CenterZ=0 NormalX=0 NormalY=0 NormalZ=1 AngleXU=0 Radius=0.5 StartAngle=0 EndAngle=1.5708
    g315: LineSegment StartX=12.5125 StartY=5.9 StartZ=0 EndX=12.5125 EndY=-5.9 EndZ=0
    g316: ArcOfCircle CenterX=12.0125 CenterY=-5.9 CenterZ=0 NormalX=0 NormalY=0 NormalZ=1 AngleXU=0 Radius=0.5 StartAngle=4.71239 EndAngle=6.28319
    g317: LineSegment StartX=-2.4875 StartY=-6.4 StartZ=0 EndX=12.0125 EndY=-6.4 EndZ=0
    g318: ArcOfCircle CenterX=-2.4875 CenterY=-5.9 CenterZ=0 NormalX=0 NormalY=0 NormalZ=1 AngleXU=0 Radius=0.5 StartAngle=3.14159 EndAngle=4.71239
    g319: LineSegment StartX=-2.9875 StartY=5.9 StartZ=0 EndX=-2.9875 EndY=-5.9 EndZ=0
    g320: ArcOfCircle CenterX=16.5625 CenterY=5.9 CenterZ=0 NormalX=0 NormalY=0 NormalZ=1 AngleXU=0 Radius=0.5 StartAngle=1.5708 EndAngle=3.14159
    g321: LineSegment StartX=16.5625 StartY=6.4 StartZ=0 EndX=31.0625 EndY=6.4 EndZ=0
    g322: ArcOfCircle CenterX=31.0625 CenterY=5.9 CenterZ=0 NormalX=0 NormalY=0 NormalZ=1 AngleXU=0 Radius=0.5 StartAngle=0 EndAngle=1.5708
    g323: LineSegment StartX=31.5625 StartY=5.9 StartZ=0 EndX=31.5625 EndY=-5.9 EndZ=0
    g324: ArcOfCircle CenterX=31.0625 CenterY=-5.9 CenterZ=0 NormalX=0 NormalY=0 NormalZ=1 AngleXU=0 Radius=0.5 StartAngle=4.71239 EndAngle=6.28319
    g325: LineSegment StartX=16.5625 StartY=-6.4 StartZ=0 EndX=31.0625 EndY=-6.4 EndZ=0
    g326: ArcOfCircle CenterX=16.5625 CenterY=-5.9 CenterZ=0 NormalX=0 NormalY=0 NormalZ=1 AngleXU=0 Radius=0.5 StartAngle=3.14159 EndAngle=4.71239
    g327: LineSegment StartX=16.0625 StartY=5.9 StartZ=0 EndX=16.0625 EndY=-5.9 EndZ=0
    g328: ArcOfCircle CenterX=35.6125 CenterY=5.9 CenterZ=0 NormalX=0 NormalY=0 NormalZ=1 AngleXU=0 Radius=0.5 StartAngle=1.5708 EndAngle=3.14159
    g329: LineSegment StartX=35.6125 StartY=6.4 StartZ=0 EndX=50.1125 EndY=6.4 EndZ=0
    g330: ArcOfCircle CenterX=50.1125 CenterY=5.9 CenterZ=0 NormalX=0 NormalY=0 NormalZ=1 AngleXU=0 Radius=0.5 StartAngle=0 EndAngle=1.5708
    g331: LineSegment StartX=50.6125 StartY=5.9 StartZ=0 EndX=50.6125 EndY=-5.9 EndZ=0
    g332: ArcOfCircle CenterX=50.1125 CenterY=-5.9 CenterZ=0 NormalX=0 NormalY=0 NormalZ=1 AngleXU=0 Radius=0.5 StartAngle=4.71239 EndAngle=6.28319
    g333: LineSegment StartX=35.6125 StartY=-6.4 StartZ=0 EndX=50.1125 EndY=-6.4 EndZ=0
    g334: ArcOfCircle CenterX=35.6125 CenterY=-5.9 CenterZ=0 NormalX=0 NormalY=0 NormalZ=1 AngleXU=0 Radius=0.5 StartAngle=3.14159 EndAngle=4.71239
    g335: LineSegment StartX=35.1125 StartY=5.9 StartZ=0 EndX=35.1125 EndY=-5.9 EndZ=0
    g336: ArcOfCircle CenterX=54.6625 CenterY=5.9 CenterZ=0 NormalX=0 NormalY=0 NormalZ=1 AngleXU=0 Radius=0.5 StartAngle=1.5708 EndAngle=3.14159
    g337: LineSegment StartX=54.6625 StartY=6.4 StartZ=0 EndX=69.1625 EndY=6.4 EndZ=0
    g338: ArcOfCircle CenterX=69.1625 CenterY=5.9 CenterZ=0 NormalX=0 NormalY=0 NormalZ=1 AngleXU=0 Radius=0.5 StartAngle=0 EndAngle=1.5708
    g339: LineSegment StartX=69.6625 StartY=5.9 StartZ=0 EndX=69.6625 EndY=-5.9 EndZ=0
    g340: ArcOfCircle CenterX=69.1625 CenterY=-5.9 CenterZ=0 NormalX=0 NormalY=0 NormalZ=1 AngleXU=0 Radius=0.5 StartAngle=4.71239 EndAngle=6.28319
    g341: LineSegment StartX=54.6625 StartY=-6.4 StartZ=0 EndX=69.1625 EndY=-6.4 EndZ=0
    g342: ArcOfCircle CenterX=54.6625 CenterY=-5.9 CenterZ=0 NormalX=0 NormalY=0 NormalZ=1 AngleXU=0 Radius=0.5 StartAngle=3.14159 EndAngle=4.71239
    g343: LineSegment StartX=54.1625 StartY=5.9 StartZ=0 EndX=54.1625 EndY=-5.9 EndZ=0
    g344: ArcOfCircle CenterX=73.7125 CenterY=5.9 CenterZ=0 NormalX=0 NormalY=0 NormalZ=1 AngleXU=0 Radius=0.5 StartAngle=1.5708 EndAngle=3.14159
    g345: LineSegment StartX=73.7125 StartY=6.4 StartZ=0 EndX=88.2125 EndY=6.4 EndZ=0
    g346: ArcOfCircle CenterX=88.2125 CenterY=5.9 CenterZ=0 NormalX=0 NormalY=0 NormalZ=1 AngleXU=0 Radius=0.5 StartAngle=0 EndAngle=1.5708
    g347: LineSegment StartX=88.7125 StartY=5.9 StartZ=0 EndX=88.7125 EndY=-5.9 EndZ=0
    g348: ArcOfCircle CenterX=88.2125 CenterY=-5.9 CenterZ=0 NormalX=0 NormalY=0 NormalZ=1 AngleXU=0 Radius=0.5 StartAngle=4.71239 EndAngle=6.28319
    g349: LineSegment StartX=73.7125 StartY=-6.4 StartZ=0 EndX=88.2125 EndY=-6.4 EndZ=0
    g350: ArcOfCircle CenterX=73.7125 CenterY=-5.9 CenterZ=0 NormalX=0 NormalY=0 NormalZ=1 AngleXU=0 Radius=0.5 StartAngle=3.14159 EndAngle=4.71239
    g351: LineSegment StartX=73.2125 StartY=5.9 StartZ=0 EndX=73.2125 EndY=-5.9 EndZ=0
    g352: ArcOfCircle CenterX=104.669 CenterY=5.9 CenterZ=0 NormalX=0 NormalY=0 NormalZ=1 AngleXU=0 Radius=0.5 StartAngle=1.5708 EndAngle=3.14159
    g353: LineSegment StartX=104.669 StartY=6.4 StartZ=0 EndX=119.169 EndY=6.4 EndZ=0
    g354: ArcOfCircle CenterX=119.169 CenterY=5.9 CenterZ=0 NormalX=0 NormalY=0 NormalZ=1 AngleXU=0 Radius=0.5 StartAngle=0 EndAngle=1.5708
    g355: LineSegment StartX=119.669 StartY=5.9 StartZ=0 EndX=119.669 EndY=-5.9 EndZ=0
    g356: ArcOfCircle CenterX=119.169 CenterY=-5.9 CenterZ=0 NormalX=0 NormalY=0 NormalZ=1 AngleXU=0 Radius=0.5 StartAngle=4.71239 EndAngle=6.28319
    g357: LineSegment StartX=104.669 StartY=-6.4 StartZ=0 EndX=119.169 EndY=-6.4 EndZ=0
    g358: ArcOfCircle CenterX=104.669 CenterY=-5.9 CenterZ=0 NormalX=0 NormalY=0 NormalZ=1 AngleXU=0 Radius=0.5 StartAngle=3.14159 EndAngle=4.71239
    g359: LineSegment StartX=104.169 StartY=5.9 StartZ=0 EndX=104.169 EndY=-5.9 EndZ=0
    g360: ArcOfCircle CenterX=96.9808 CenterY=5.5 CenterZ=0 NormalX=0 NormalY=0 NormalZ=1 AngleXU=0 Radius=0.5 StartAngle=1.5708 EndAngle=3.14159
    g361: LineSegment StartX=96.9808 StartY=6 StartZ=0 EndX=102.981 EndY=6 EndZ=0
    g362: ArcOfCircle CenterX=102.981 CenterY=5.5 CenterZ=0 NormalX=0 NormalY=0 NormalZ=1 AngleXU=0 Radius=0.5 StartAngle=0 EndAngle=1.5708
    g363: LineSegment StartX=103.481 StartY=5.5 StartZ=0 EndX=103.481 EndY=-8.5 EndZ=0
    g364: ArcOfCircle CenterX=102.981 CenterY=-8.5 CenterZ=0 NormalX=0 NormalY=0 NormalZ=1 AngleXU=0 Radius=0.5 StartAngle=4.71239 EndAngle=6.28319
    g365: LineSegment StartX=96.9808 StartY=-9 StartZ=0 EndX=102.981 EndY=-9 EndZ=0
    g366: ArcOfCircle CenterX=96.9808 CenterY=-8.5 CenterZ=0 NormalX=0 NormalY=0 NormalZ=1 AngleXU=0 Radius=0.5 StartAngle=3.14159 EndAngle=4.71239
    g367: LineSegment StartX=96.4808 StartY=5.5 StartZ=0 EndX=96.4808 EndY=-8.5 EndZ=0
    g368: ArcOfCircle CenterX=120.857 CenterY=5.5 CenterZ=0 NormalX=0 NormalY=0 NormalZ=1 AngleXU=0 Radius=0.5 StartAngle=1.5708 EndAngle=3.14159
    g369: LineSegment StartX=120.857 StartY=6 StartZ=0 EndX=126.857 EndY=6 EndZ=0
    g370: ArcOfCircle CenterX=126.857 CenterY=5.5 CenterZ=0 NormalX=0 NormalY=0 NormalZ=1 AngleXU=0 Radius=0.5 StartAngle=0 EndAngle=1.5708
    g371: LineSegment StartX=127.357 StartY=5.5 StartZ=0 EndX=127.357 EndY=-8.5 EndZ=0
    g372: ArcOfCircle CenterX=126.857 CenterY=-8.5 CenterZ=0 NormalX=0 NormalY=0 NormalZ=1 AngleXU=0 Radius=0.5 StartAngle=4.71239 EndAngle=6.28319
    g373: LineSegment StartX=120.857 StartY=-9 StartZ=0 EndX=126.857 EndY=-9 EndZ=0
    g374: ArcOfCircle CenterX=120.857 CenterY=-8.5 CenterZ=0 NormalX=0 NormalY=0 NormalZ=1 AngleXU=0 Radius=0.5 StartAngle=3.14159 EndAngle=4.71239
    g375: LineSegment StartX=120.357 StartY=5.5 StartZ=0 EndX=120.357 EndY=-8.5 EndZ=0
    g376: ArcOfCircle CenterX=135.625 CenterY=5.9 CenterZ=0 NormalX=0 NormalY=0 NormalZ=1 AngleXU=0 Radius=0.5 StartAngle=1.5708 EndAngle=3.14159
    g377: LineSegment StartX=135.625 StartY=6.4 StartZ=0 EndX=150.125 EndY=6.4 EndZ=0
    g378: ArcOfCircle CenterX=150.125 CenterY=5.9 CenterZ=0 NormalX=0 NormalY=0 NormalZ=1 AngleXU=0 Radius=0.5 StartAngle=0 EndAngle=1.5708
    g379: LineSegment StartX=150.625 StartY=5.9 StartZ=0 EndX=150.625 EndY=-5.9 EndZ=0
    g380: ArcOfCircle CenterX=150.125 CenterY=-5.9 CenterZ=0 NormalX=0 NormalY=0 NormalZ=1 AngleXU=0 Radius=0.5 StartAngle=4.71239 EndAngle=6.28319
    g381: LineSegment StartX=135.625 StartY=-6.4 StartZ=0 EndX=150.125 EndY=-6.4 EndZ=0
    g382: ArcOfCircle CenterX=135.625 CenterY=-5.9 CenterZ=0 NormalX=0 NormalY=0 NormalZ=1 AngleXU=0 Radius=0.5 StartAngle=3.14159 EndAngle=4.71239
    g383: LineSegment StartX=135.125 StartY=5.9 StartZ=0 EndX=135.125 EndY=-5.9 EndZ=0
    g384: ArcOfCircle CenterX=-138.219 CenterY=-13.15 CenterZ=0 NormalX=0 NormalY=0 NormalZ=1 AngleXU=0 Radius=0.5 StartAngle=1.5708 EndAngle=3.14159
    g385: LineSegment StartX=-138.219 StartY=-12.65 StartZ=0 EndX=-123.719 EndY=-12.65 EndZ=0
    g386: ArcOfCircle CenterX=-123.719 CenterY=-13.15 CenterZ=0 NormalX=0 NormalY=0 NormalZ=1 AngleXU=0 Radius=0.5 StartAngle=0 EndAngle=1.5708
    g387: LineSegment StartX=-123.219 StartY=-13.15 StartZ=0 EndX=-123.219 EndY=-24.95 EndZ=0
    g388: ArcOfCircle CenterX=-123.719 CenterY=-24.95 CenterZ=0 NormalX=0 NormalY=0 NormalZ=1 AngleXU=0 Radius=0.5 StartAngle=4.71239 EndAngle=6.28319
    g389: LineSegment StartX=-138.219 StartY=-25.45 StartZ=0 EndX=-123.719 EndY=-25.45 EndZ=0
    g390: ArcOfCircle CenterX=-138.219 CenterY=-24.95 CenterZ=0 NormalX=0 NormalY=0 NormalZ=1 AngleXU=0 Radius=0.5 StartAngle=3.14159 EndAngle=4.71239
    g391: LineSegment StartX=-138.719 StartY=-13.15 StartZ=0 EndX=-138.719 EndY=-24.95 EndZ=0
    g392: ArcOfCircle CenterX=-145.907 CenterY=-13.55 CenterZ=0 NormalX=0 NormalY=0 NormalZ=1 AngleXU=0 Radius=0.5 StartAngle=1.5708 EndAngle=3.14159
    g393: LineSegment StartX=-145.907 StartY=-13.05 StartZ=0 EndX=-139.907 EndY=-13.05 EndZ=0
    g394: ArcOfCircle CenterX=-139.907 CenterY=-13.55 CenterZ=0 NormalX=0 NormalY=0 NormalZ=1 AngleXU=0 Radius=0.5 StartAngle=0 EndAngle=1.5708
    g395: LineSegment StartX=-139.407 StartY=-13.55 StartZ=0 EndX=-139.407 EndY=-27.55 EndZ=0
    g396: ArcOfCircle CenterX=-139.907 CenterY=-27.55 CenterZ=0 NormalX=0 NormalY=0 NormalZ=1 AngleXU=0 Radius=0.5 StartAngle=4.71239 EndAngle=6.28319
    g397: LineSegment StartX=-145.907 StartY=-28.05 StartZ=0 EndX=-139.907 EndY=-28.05 EndZ=0
    g398: ArcOfCircle CenterX=-145.907 CenterY=-27.55 CenterZ=0 NormalX=0 NormalY=0 NormalZ=1 AngleXU=0 Radius=0.5 StartAngle=3.14159 EndAngle=4.71239
    g399: LineSegment StartX=-146.407 StartY=-13.55 StartZ=0 EndX=-146.407 EndY=-27.55 EndZ=0
    ... +288 more geometry lines
  constraints (80):
    c: Tangent(g686,g687) = 1.5708
    c: Tangent(g685,g686) = 1.5708
    c: Tangent(g683,g684) = 1.5708
    c: Tangent(g684,g685) = 1.5708
    c: Tangent(g681,g682) = 1.5708
    c: Tangent(g680,g681) = 1.5708
    c: Tangent(g679,g680) = 1.5708
    c: Tangent(g678,g679) = 1.5708
    c: Tangent(g677,g678) = 1.5708
    c: Tangent(g676,g677) = 1.5708
    c: Tangent(g675,g676) = 1.5708
    c: Tangent(g674,g675) = 1.5708
    c: Tangent(g673,g674) = 1.5708
    c: Tangent(g672,g673) = 1.5708
    c: Tangent(g671,g672) = 1.5708
    c: Tangent(g669,g670) = 1.5708
    c: Tangent(g670,g671) = 1.5708
    c: Tangent(g668,g669) = 1.5708
    c: Tangent(g667,g668) = 1.5708
    c: Tangent(g666,g667) = 1.5708
    c: Tangent(g665,g666) = 1.5708
    c: Tangent(g664,g665) = 1.5708
    c: Tangent(g663,g664) = 1.5708
    c: Tangent(g662,g663) = 1.5708
    c: Tangent(g661,g662) = 1.5708
    c: Tangent(g660,g661) = 1.5708
    c: Tangent(g659,g660) = 1.5708
    c: Tangent(g657,g658) = 1.5708
    c: Tangent(g658,g659) = 1.5708
    c: Tangent(g656,g657) = 1.5708
    c: Tangent(g655,g656) = 1.5708
    c: Tangent(g654,g655) = 1.5708
    c: Tangent(g653,g654) = 1.5708
    c: Tangent(g652,g653) = 1.5708
    c: Tangent(g651,g652) = 1.5708
    c: Tangent(g650,g651) = 1.5708
    c: Tangent(g649,g650) = 1.5708
    c: Tangent(g648,g649) = 1.5708
    c: Tangent(g647,g648) = 1.5708
    c: Tangent(g646,g647) = 1.5708
    c: Tangent(g645,g646) = 1.5708
    c: Tangent(g644,g645) = 1.5708
    c: Tangent(g643,g644) = 1.5708
    c: Tangent(g642,g643) = 1.5708
    c: Tangent(g641,g642) = 1.5708
    c: Tangent(g640,g641) = 1.5708
    c: Tangent(g639,g640) = 1.5708
    c: Tangent(g638,g639) = 1.5708
    c: Tangent(g637,g638) = 1.5708
    c: Tangent(g633,g634) = 1.5708
    c: Tangent(g634,g635) = 1.5708
    c: Tangent(g635,g636) = 1.5708
    c: Tangent(g636,g637) = 1.5708
    c: Tangent(g628,g629) = 1.5708
    c: Tangent(g629,g630) = 1.5708
    c: Tangent(g630,g631) = 1.5708
    c: Tangent(g631,g632) = 1.5708
    c: Tangent(g632,g633) = 1.5708
    c: Tangent(g627,g628) = 1.5708
    c: Tangent(g626,g627) = 1.5708
    c: Tangent(g625,g626) = 1.5708
    c: Tangent(g621,g622) = 1.5708
    c: Tangent(g622,g623) = 1.5708
    c: Tangent(g623,g624) = 1.5708
    c: Tangent(g624,g625) = 1.5708
    c: Tangent(g620,g621) = 1.5708
    c: Tangent(g619,g620) = 1.5708
    c: Tangent(g618,g619) = 1.5708
    c: Tangent(g617,g618) = 1.5708
    c: Tangent(g616,g617) = 1.5708
    c: Tangent(g615,g616) = 1.5708
    c: Tangent(g613,g614) = 1.5708
    c: Tangent(g614,g615) = 1.5708
    c: Tangent(g612,g613) = 1.5708
    c: Tangent(g611,g612) = 1.5708
    c: Tangent(g610,g611) = 1.5708
    c: Tangent(g609,g610) = 1.5708
    c: Tangent(g608,g609) = 1.5708
    c: Tangent(g608,g687) = 1.5708
    c: Tangent(g682,g683) = 1.5708
FEATURE [PartDesign::Pad] Pad
  Direction = (0,0,1)
  Length = 1.6
  Length2 = 10
  Profile = -> Sketch
  ReferenceAxis = -> Sketch [N_Axis]
  Type = 0
FEATURE [PartDesign::Body] Body
  Group = -> [Sketch,Pad]
  Origin = -> Origin
  Tip = -> Pad
